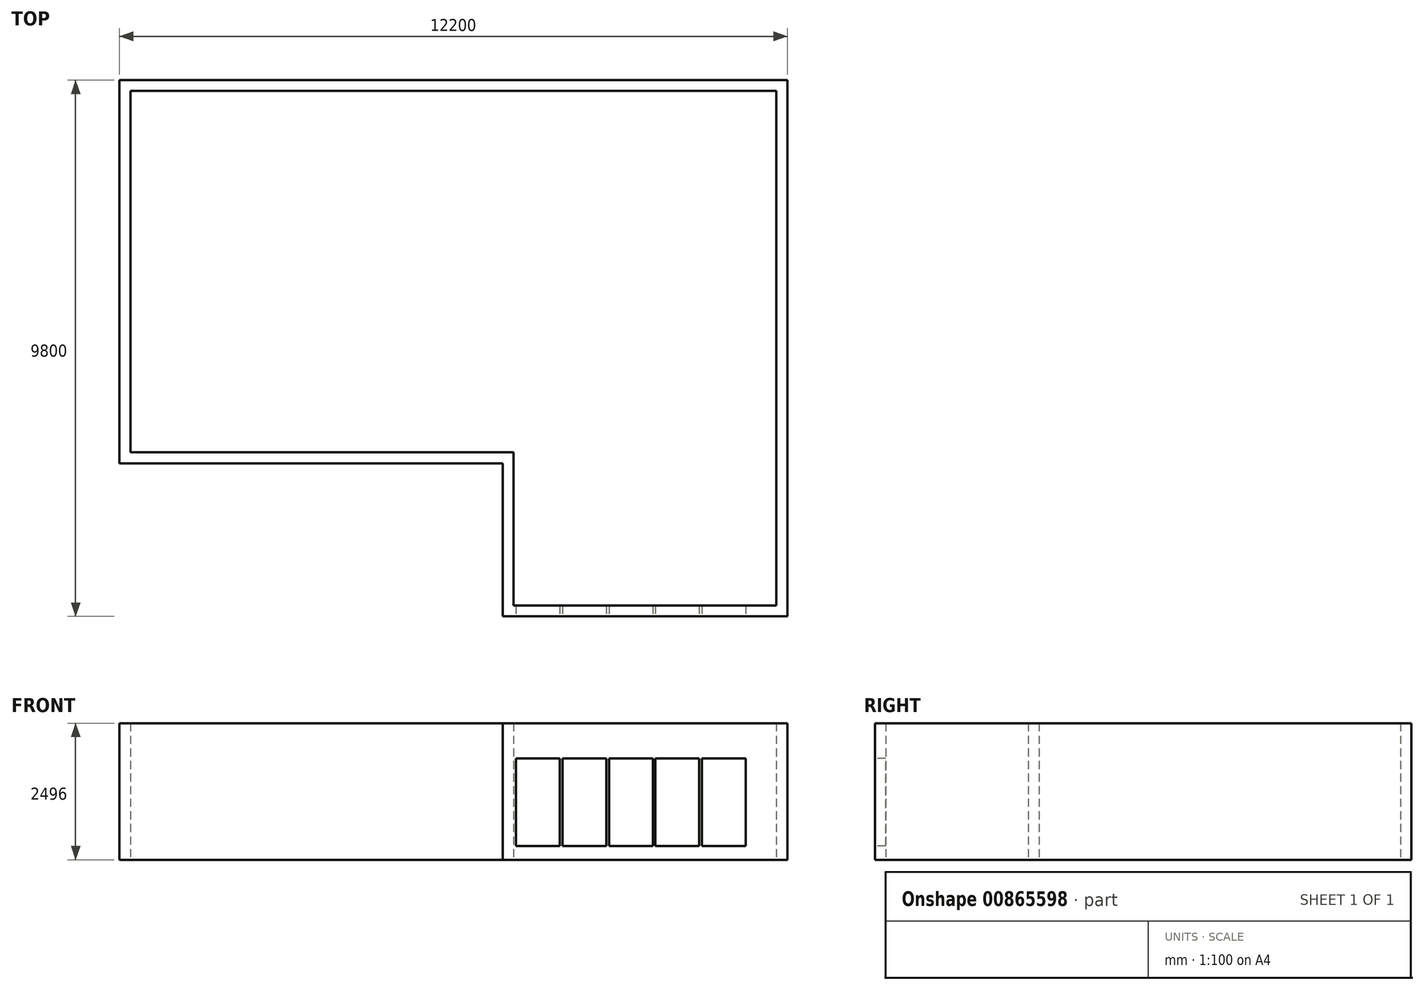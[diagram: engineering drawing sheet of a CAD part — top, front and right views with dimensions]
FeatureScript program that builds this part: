
annotation { "Feature Type Name" : "Feature", "Feature Type Description" : "" }
export const myFeature = defineFeature(function(context is Context, id is Id, definition is map)
    precondition{}
    {
        {
            var Q0;
            Q0=qCreatedBy(makeId("Top.planeOp"),FACE);
            var sketch = newSketch(context, id + "F0", { "sketchPlane" : qUnion([Q0])});
            skLineSegment(sketch, "E0.bottom", {"start": v(-1374.6, -4056.54) * mm, "end": v(3825.4, -4056.54) * mm});
            skLineSegment(sketch, "E0.top", {"start": v(-8374.6, 5743.46) * mm, "end": v(3825.4, 5743.46) * mm});
            skLineSegment(sketch, "E0.left", {"start": v(-8374.6, -1256.54) * mm, "end": v(-8374.6, 5743.46) * mm});
            skLineSegment(sketch, "E0.right", {"start": v(3825.4, -4056.54) * mm, "end": v(3825.4, 5743.46) * mm});
            skLineSegment(sketch, "E1", {"start": v(-8374.6, -1256.54) * mm, "end": v(-1374.6, -1256.54) * mm});
            skLineSegment(sketch, "E2", {"start": v(-1374.6, -1256.54) * mm, "end": v(-1374.6, -4056.54) * mm});
            skLineSegment(sketch, "E3.0", {"start": v(-8176.6, -1058.54) * mm, "end": v(-8176.6, 5545.46) * mm});
            skLineSegment(sketch, "E3.1", {"start": v(3627.4, -3858.54) * mm, "end": v(3627.4, 5545.46) * mm});
            skLineSegment(sketch, "E3.2", {"start": v(-1176.6, -3858.54) * mm, "end": v(3627.4, -3858.54) * mm});
            skLineSegment(sketch, "E3.3", {"start": v(-8176.6, 5545.46) * mm, "end": v(3627.4, 5545.46) * mm});
            skLineSegment(sketch, "E3.4", {"start": v(-1176.6, -1058.54) * mm, "end": v(-1176.6, -3858.54) * mm});
            skLineSegment(sketch, "E3.5", {"start": v(-8176.6, -1058.54) * mm, "end": v(-1176.6, -1058.54) * mm});
            skSolve(sketch);
        }
        {
            var Q0;
            Q0=makeQuery(id+"F0.imprint","IMPRINT",FACE,{"disambiguationData":[TD([[makeQuery(id+"F0.imprint","IMPRINT",EDGE,{"derivedFrom":sQuery(id+"F0.wireOp",EDGE,"E0.bottom")}),1.0]])]});
            extrude(context, id + "F1", {"entities" : qUnion([Q0]), "depth" : 2496 * mm, "offsetDistance" : 25 * mm});
        }
        {
            var Q0;
            Q0=makeQuery(id+"F1.opExtrude","SWEPT_FACE",FACE,{"disambiguationData":[OSD([sQuery(id+"F0.wireOp",EDGE,"E0.bottom")])]});
            var sketch = newSketch(context, id + "F2", { "sketchPlane" : qUnion([Q0])});
            skLineSegment(sketch, "E4.bottom", {"start": v(-1128.6, 1852) * mm, "end": v(-328.6, 1852) * mm});
            skLineSegment(sketch, "E4.top", {"start": v(-1128.6, 252) * mm, "end": v(-328.6, 252) * mm});
            skLineSegment(sketch, "E4.left", {"start": v(-1128.6, 1852) * mm, "end": v(-1128.6, 252) * mm});
            skLineSegment(sketch, "E4.right", {"start": v(-328.6, 1852) * mm, "end": v(-328.6, 252) * mm});
            skLineSegment(sketch, "E5", {"start": v(-1176.6, 2496) * mm, "end": v(-1176.6, 0) * mm});
            skLineSegment(sketch, "E6.1.0.0", {"start": v(519.4, 1852) * mm, "end": v(519.4, 252) * mm});
            skLineSegment(sketch, "E6.1.0.1", {"start": v(-280.6, 1852) * mm, "end": v(519.4, 1852) * mm});
            skLineSegment(sketch, "E6.1.0.2", {"start": v(-280.6, 1852) * mm, "end": v(-280.6, 252) * mm});
            skLineSegment(sketch, "E6.1.0.3", {"start": v(-280.6, 252) * mm, "end": v(519.4, 252) * mm});
            skLineSegment(sketch, "E6.2.0.0", {"start": v(1367.4, 1852) * mm, "end": v(1367.4, 252) * mm});
            skLineSegment(sketch, "E6.2.0.1", {"start": v(567.4, 1852) * mm, "end": v(1367.4, 1852) * mm});
            skLineSegment(sketch, "E6.2.0.2", {"start": v(567.4, 1852) * mm, "end": v(567.4, 252) * mm});
            skLineSegment(sketch, "E6.2.0.3", {"start": v(567.4, 252) * mm, "end": v(1367.4, 252) * mm});
            skLineSegment(sketch, "E6.3.0.0", {"start": v(2215.4, 1852) * mm, "end": v(2215.4, 252) * mm});
            skLineSegment(sketch, "E6.3.0.1", {"start": v(1415.4, 1852) * mm, "end": v(2215.4, 1852) * mm});
            skLineSegment(sketch, "E6.3.0.2", {"start": v(1415.4, 1852) * mm, "end": v(1415.4, 252) * mm});
            skLineSegment(sketch, "E6.3.0.3", {"start": v(1415.4, 252) * mm, "end": v(2215.4, 252) * mm});
            skLineSegment(sketch, "E6.4.0.0", {"start": v(3063.4, 1852) * mm, "end": v(3063.4, 252) * mm});
            skLineSegment(sketch, "E6.4.0.1", {"start": v(2263.4, 1852) * mm, "end": v(3063.4, 1852) * mm});
            skLineSegment(sketch, "E6.4.0.2", {"start": v(2263.4, 1852) * mm, "end": v(2263.4, 252) * mm});
            skLineSegment(sketch, "E6.4.0.3", {"start": v(2263.4, 252) * mm, "end": v(3063.4, 252) * mm});
            skLineSegment(sketch, "E6.direction1", {"start": v(-328.6, 252) * mm, "end": v(519.4, 252) * mm, "construction": true});
            skSolve(sketch);
        }
        {
            var Q0;
            Q0=makeQuery(id+"F2.imprint","IMPRINT",FACE,{"disambiguationData":[TD([[makeQuery(id+"F2.imprint","IMPRINT",EDGE,{"derivedFrom":sQuery(id+"F2.wireOp",EDGE,"E6.1.0.0")}),-1.0]])]});
            var Q1;
            Q1=makeQuery(id+"F2.imprint","IMPRINT",FACE,{"disambiguationData":[TD([[makeQuery(id+"F2.imprint","IMPRINT",EDGE,{"derivedFrom":sQuery(id+"F2.wireOp",EDGE,"E4.bottom")}),-1.0]])]});
            var Q2;
            Q2=makeQuery(id+"F2.imprint","IMPRINT",FACE,{"disambiguationData":[TD([[makeQuery(id+"F2.imprint","IMPRINT",EDGE,{"derivedFrom":sQuery(id+"F2.wireOp",EDGE,"E6.2.0.0")}),-1.0]])]});
            var Q3;
            Q3=makeQuery(id+"F2.imprint","IMPRINT",FACE,{"disambiguationData":[TD([[makeQuery(id+"F2.imprint","IMPRINT",EDGE,{"derivedFrom":sQuery(id+"F2.wireOp",EDGE,"E6.3.0.0")}),-1.0]])]});
            var Q4;
            Q4=makeQuery(id+"F2.imprint","IMPRINT",FACE,{"disambiguationData":[TD([[makeQuery(id+"F2.imprint","IMPRINT",EDGE,{"derivedFrom":sQuery(id+"F2.wireOp",EDGE,"E6.4.0.0")}),-1.0]])]});
            extrude(context, id + "F3", {"entities" : qUnion([Q0, Q1, Q2, Q3, Q4]), "operationType" : NewBodyOperationType.REMOVE, "oppositeDirection" : true, "depth" : 200 * mm, "offsetDistance" : 25 * mm});
        }
    });
